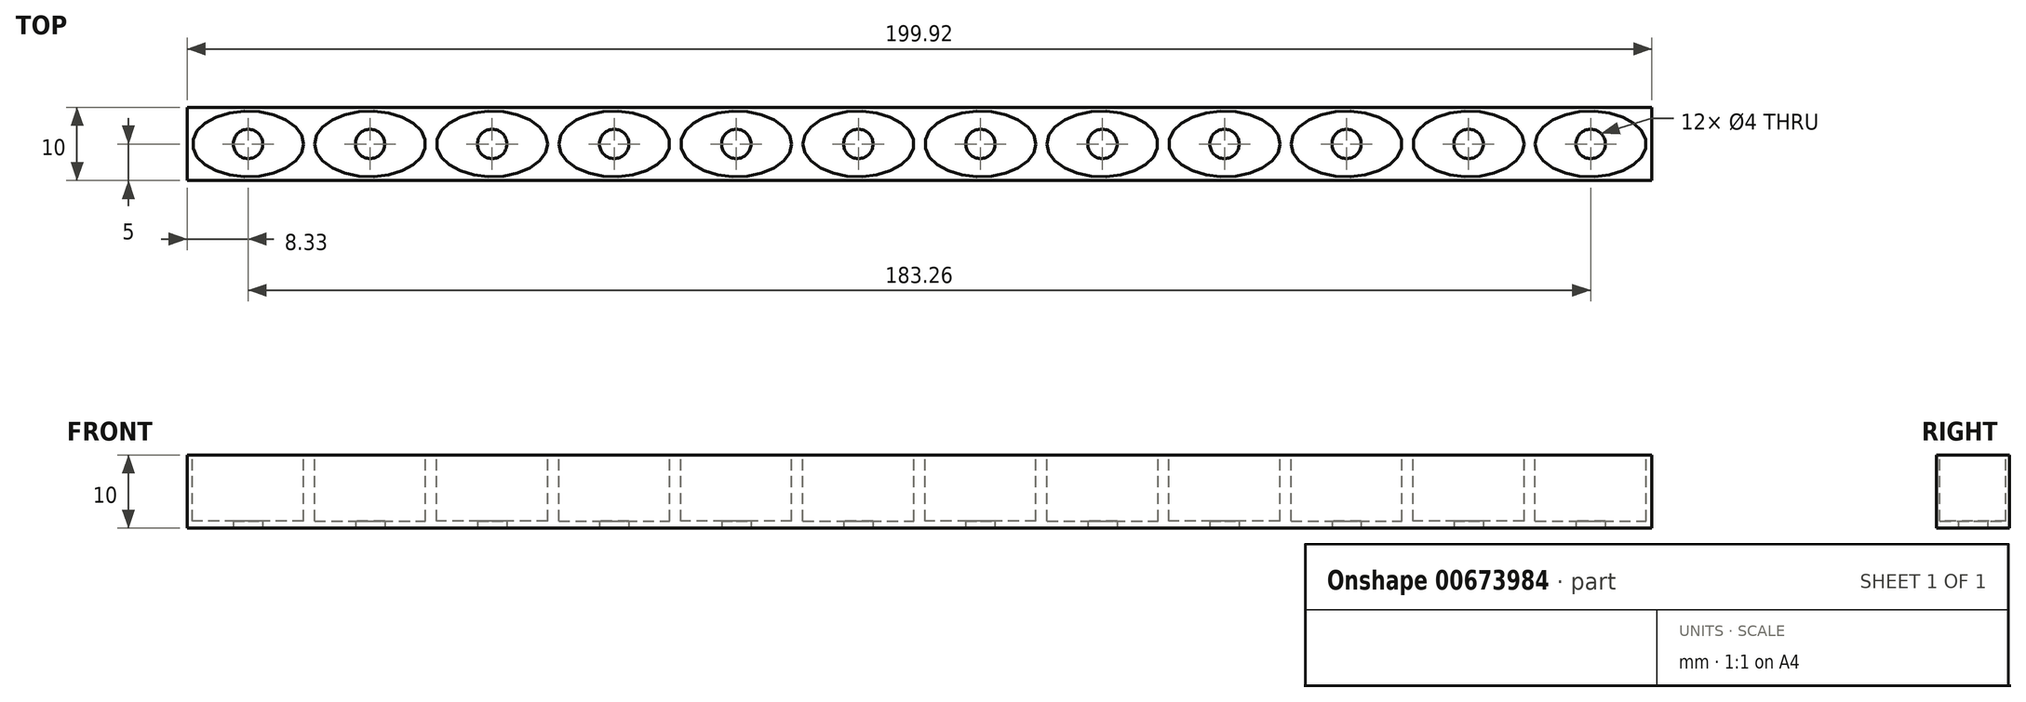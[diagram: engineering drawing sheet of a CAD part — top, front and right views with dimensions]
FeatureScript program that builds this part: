
annotation { "Feature Type Name" : "Feature", "Feature Type Description" : "" }
export const myFeature = defineFeature(function(context is Context, id is Id, definition is map)
    precondition{}
    {
        {
            var Q0;
            Q0=qCreatedBy(makeId("Front.planeOp"),FACE);
            var sketch = newSketch(context, id + "F0", { "sketchPlane" : qUnion([Q0])});
            skLineSegment(sketch, "E0.bottom", {"start": v(-8.33, 5) * mm, "end": v(8.33, 5) * mm});
            skLineSegment(sketch, "E0.top", {"start": v(-8.33, -5) * mm, "end": v(8.33, -5) * mm});
            skLineSegment(sketch, "E0.left", {"start": v(-8.33, 5) * mm, "end": v(-8.33, -5) * mm});
            skLineSegment(sketch, "E0.right", {"start": v(8.33, 5) * mm, "end": v(8.33, -5) * mm});
            skPoint(sketch, "E0.middle", {"position": v(0, 0) * mm});
            skCircle(sketch, "E1", {"center": v(0, 0) * mm, "radius": 2 * mm});
            skLineSegment(sketch, "E2.bottom", {"start": v(-24.99, 5) * mm, "end": v(-8.33, 5) * mm});
            skLineSegment(sketch, "E2.top", {"start": v(-24.99, -5) * mm, "end": v(-8.33, -5) * mm});
            skLineSegment(sketch, "E2.left", {"start": v(-24.99, 5) * mm, "end": v(-24.99, -5) * mm});
            skPoint(sketch, "E2.middle", {"position": v(-16.66, 0) * mm});
            skCircle(sketch, "E3", {"center": v(-16.66, 0) * mm, "radius": 2 * mm});
            skLineSegment(sketch, "E4.bottom", {"start": v(8.33, 5) * mm, "end": v(25, 5) * mm});
            skLineSegment(sketch, "E4.top", {"start": v(8.33, -5) * mm, "end": v(25, -5) * mm});
            skLineSegment(sketch, "E4.right", {"start": v(25, 5) * mm, "end": v(25, -5) * mm});
            skPoint(sketch, "E4.middle", {"position": v(16.66, 0) * mm});
            skCircle(sketch, "E5", {"center": v(16.66, 0) * mm, "radius": 2 * mm});
            skLineSegment(sketch, "E6.bottom", {"start": v(-58.31, 5) * mm, "end": v(-41.65, 5) * mm});
            skLineSegment(sketch, "E6.top", {"start": v(-58.3, -5) * mm, "end": v(-41.65, -5) * mm});
            skLineSegment(sketch, "E6.left", {"start": v(-58.3, 5) * mm, "end": v(-58.3, -5) * mm});
            skLineSegment(sketch, "E6.right", {"start": v(-41.65, 5) * mm, "end": v(-41.65, -5) * mm});
            skPoint(sketch, "E6.middle", {"position": v(-49.98, 0) * mm});
            skCircle(sketch, "E7", {"center": v(-49.98, 0) * mm, "radius": 2 * mm});
            skLineSegment(sketch, "E8.bottom", {"start": v(-74.97, 5) * mm, "end": v(-58.31, 5) * mm});
            skLineSegment(sketch, "E8.top", {"start": v(-74.97, -5) * mm, "end": v(-58.3, -5) * mm});
            skLineSegment(sketch, "E8.left", {"start": v(-74.97, 5) * mm, "end": v(-74.97, -5) * mm});
            skPoint(sketch, "E8.middle", {"position": v(-66.64, 0) * mm});
            skCircle(sketch, "E9", {"center": v(-66.64, 0) * mm, "radius": 2 * mm});
            skLineSegment(sketch, "E10.bottom", {"start": v(-41.65, 5) * mm, "end": v(-24.99, 5) * mm});
            skLineSegment(sketch, "E10.top", {"start": v(-41.65, -5) * mm, "end": v(-25, -5) * mm});
            skPoint(sketch, "E10.middle", {"position": v(-33.32, 0) * mm});
            skCircle(sketch, "E11", {"center": v(-33.32, 0) * mm, "radius": 2 * mm});
            skLineSegment(sketch, "E12.bottom", {"start": v(41.65, 5) * mm, "end": v(58.31, 5) * mm});
            skLineSegment(sketch, "E12.top", {"start": v(41.65, -5) * mm, "end": v(58.31, -5) * mm});
            skLineSegment(sketch, "E12.left", {"start": v(41.65, 5) * mm, "end": v(41.65, -5) * mm});
            skLineSegment(sketch, "E12.right", {"start": v(58.31, 5) * mm, "end": v(58.31, -5) * mm});
            skPoint(sketch, "E12.middle", {"position": v(49.98, 0) * mm});
            skCircle(sketch, "E13", {"center": v(49.98, 0) * mm, "radius": 2 * mm});
            skLineSegment(sketch, "E14.bottom", {"start": v(25, 5) * mm, "end": v(41.65, 5) * mm});
            skLineSegment(sketch, "E14.top", {"start": v(25, -5) * mm, "end": v(41.65, -5) * mm});
            skPoint(sketch, "E14.middle", {"position": v(33.32, 0) * mm});
            skCircle(sketch, "E15", {"center": v(33.32, 0) * mm, "radius": 2 * mm});
            skLineSegment(sketch, "E16.bottom", {"start": v(58.31, 5) * mm, "end": v(74.97, 5) * mm});
            skLineSegment(sketch, "E16.top", {"start": v(58.31, -5) * mm, "end": v(74.97, -5) * mm});
            skLineSegment(sketch, "E16.right", {"start": v(74.97, 5) * mm, "end": v(74.97, -5) * mm});
            skPoint(sketch, "E16.middle", {"position": v(66.64, 0) * mm});
            skCircle(sketch, "E17", {"center": v(66.64, 0) * mm, "radius": 2 * mm});
            skLineSegment(sketch, "E18.bottom", {"start": v(-108.29, 5) * mm, "end": v(-91.63, 5) * mm});
            skLineSegment(sketch, "E18.top", {"start": v(-108.29, -5) * mm, "end": v(-91.63, -5) * mm});
            skLineSegment(sketch, "E18.left", {"start": v(-108.29, 5) * mm, "end": v(-108.29, -5) * mm});
            skLineSegment(sketch, "E18.right", {"start": v(-91.63, 5) * mm, "end": v(-91.63, -5) * mm});
            skPoint(sketch, "E18.middle", {"position": v(-99.96, 0) * mm});
            skCircle(sketch, "E19", {"center": v(-99.96, 0) * mm, "radius": 2 * mm});
            skLineSegment(sketch, "E20.bottom", {"start": v(-124.95, 5) * mm, "end": v(-108.29, 5) * mm});
            skLineSegment(sketch, "E20.top", {"start": v(-124.95, -5) * mm, "end": v(-108.29, -5) * mm});
            skLineSegment(sketch, "E20.left", {"start": v(-124.95, 5) * mm, "end": v(-124.95, -5) * mm});
            skPoint(sketch, "E20.middle", {"position": v(-116.62, 0) * mm});
            skCircle(sketch, "E21", {"center": v(-116.62, 0) * mm, "radius": 2 * mm});
            skLineSegment(sketch, "E22.bottom", {"start": v(-91.63, 5) * mm, "end": v(-74.97, 5) * mm});
            skLineSegment(sketch, "E22.top", {"start": v(-91.63, -5) * mm, "end": v(-74.97, -5) * mm});
            skPoint(sketch, "E22.middle", {"position": v(-83.3, 0) * mm});
            skCircle(sketch, "E23", {"center": v(-83.3, 0) * mm, "radius": 2 * mm});
            skSolve(sketch);
        }
        {
            var Q0;
            Q0 = qSketchRegion(id + "F0", true);
            extrude(context, id + "F1", {"entities" : qUnion([Q0]), "depth" : 10 * mm, "offsetDistance" : 25 * mm});
        }
        {
            var Q0;
            Q0=makeQuery(id+"F1.opExtrude","CAP_FACE",FACE,{"disambiguationData":[OSD([sQuery(id+"F0.wireOp",EDGE,"E0.bottom"),sQuery(id+"F0.wireOp",EDGE,"E0.top"),sQuery(id+"F0.wireOp",EDGE,"E1"),sQuery(id+"F0.wireOp",EDGE,"E2.bottom"),sQuery(id+"F0.wireOp",EDGE,"E2.top"),sQuery(id+"F0.wireOp",EDGE,"E3"),sQuery(id+"F0.wireOp",EDGE,"E4.bottom"),sQuery(id+"F0.wireOp",EDGE,"E4.top"),sQuery(id+"F0.wireOp",EDGE,"E5"),sQuery(id+"F0.wireOp",EDGE,"E6.bottom"),sQuery(id+"F0.wireOp",EDGE,"E6.top"),sQuery(id+"F0.wireOp",EDGE,"E7"),sQuery(id+"F0.wireOp",EDGE,"E8.bottom"),sQuery(id+"F0.wireOp",EDGE,"E8.top"),sQuery(id+"F0.wireOp",EDGE,"E9"),sQuery(id+"F0.wireOp",EDGE,"E10.bottom"),sQuery(id+"F0.wireOp",EDGE,"E10.top"),sQuery(id+"F0.wireOp",EDGE,"E11"),sQuery(id+"F0.wireOp",EDGE,"E12.bottom"),sQuery(id+"F0.wireOp",EDGE,"E12.top"),sQuery(id+"F0.wireOp",EDGE,"E13"),sQuery(id+"F0.wireOp",EDGE,"E14.bottom"),sQuery(id+"F0.wireOp",EDGE,"E14.top"),sQuery(id+"F0.wireOp",EDGE,"E15"),sQuery(id+"F0.wireOp",EDGE,"E16.bottom"),sQuery(id+"F0.wireOp",EDGE,"E16.top"),sQuery(id+"F0.wireOp",EDGE,"E16.right"),sQuery(id+"F0.wireOp",EDGE,"E17"),sQuery(id+"F0.wireOp",EDGE,"E18.bottom"),sQuery(id+"F0.wireOp",EDGE,"E18.top"),sQuery(id+"F0.wireOp",EDGE,"E19"),sQuery(id+"F0.wireOp",EDGE,"E20.bottom"),sQuery(id+"F0.wireOp",EDGE,"E20.top"),sQuery(id+"F0.wireOp",EDGE,"E20.left"),sQuery(id+"F0.wireOp",EDGE,"E21"),sQuery(id+"F0.wireOp",EDGE,"E22.bottom"),sQuery(id+"F0.wireOp",EDGE,"E22.top"),sQuery(id+"F0.wireOp",EDGE,"E23")])],"isStart":false});
            cPlane(context, id + "F2", {"entities" : qUnion([Q0]), "cplaneType" : CPlaneType.OFFSET, "offset" : 0 * mm, "width" : 150 * mm, "height" : 150 * mm});
        }
        {
            var Q0;
            Q0=qCreatedBy(id+"F2.planeOp",FACE);
            var sketch = newSketch(context, id + "F3", { "sketchPlane" : qUnion([Q0])});
            skEllipse(sketch, "E24", {"center": v(0, 0) * mm, "majorRadius": 7.58 * mm, "minorRadius": 4.5 * mm, "majorAxis": v(-1, 0)});
            skEllipse(sketch, "E25.MirrorC", {"center": v(16.66, 0) * mm, "majorRadius": 7.58 * mm, "minorRadius": 4.5 * mm, "majorAxis": v(1, 0)});
            skEllipse(sketch, "E26.MirrorC", {"center": v(33.32, 0) * mm, "majorRadius": 7.58 * mm, "minorRadius": 4.5 * mm, "majorAxis": v(-1, 0)});
            skEllipse(sketch, "E27.MirrorC", {"center": v(49.98, 0) * mm, "majorRadius": 7.58 * mm, "minorRadius": 4.5 * mm, "majorAxis": v(1, 0)});
            skEllipse(sketch, "E28.MirrorC", {"center": v(66.64, 0) * mm, "majorRadius": 7.58 * mm, "minorRadius": 4.5 * mm, "majorAxis": v(-1, 0)});
            skEllipse(sketch, "E29.MirrorC", {"center": v(-16.66, 0) * mm, "majorRadius": 7.58 * mm, "minorRadius": 4.5 * mm, "majorAxis": v(1, 0)});
            skEllipse(sketch, "E30.MirrorC", {"center": v(-33.32, 0) * mm, "majorRadius": 7.58 * mm, "minorRadius": 4.5 * mm, "majorAxis": v(-1, 0)});
            skEllipse(sketch, "E31.MirrorC", {"center": v(-49.98, 0) * mm, "majorRadius": 7.58 * mm, "minorRadius": 4.5 * mm, "majorAxis": v(1, 0)});
            skEllipse(sketch, "E32.MirrorC", {"center": v(-66.64, 0) * mm, "majorRadius": 7.58 * mm, "minorRadius": 4.5 * mm, "majorAxis": v(-1, 0)});
            skEllipse(sketch, "E33.MirrorC", {"center": v(-83.3, 0) * mm, "majorRadius": 7.58 * mm, "minorRadius": 4.5 * mm, "majorAxis": v(1, 0)});
            skEllipse(sketch, "E34.MirrorC", {"center": v(-99.96, 0) * mm, "majorRadius": 7.58 * mm, "minorRadius": 4.5 * mm, "majorAxis": v(-1, 0)});
            skEllipse(sketch, "E35.MirrorC", {"center": v(-116.62, 0) * mm, "majorRadius": 7.58 * mm, "minorRadius": 4.5 * mm, "majorAxis": v(1, 0)});
            skSolve(sketch);
        }
        {
            var Q0;
            Q0=makeQuery(id+"F3.imprint","IMPRINT",FACE,{"disambiguationData":[TD([[makeQuery(id+"F3.imprint","IMPRINT",EDGE,{"derivedFrom":sQuery(id+"F3.wireOp",EDGE,"E33.MirrorC")}),1.0]])]});
            var Q1;
            Q1=makeQuery(id+"F3.imprint","IMPRINT",FACE,{"disambiguationData":[TD([[makeQuery(id+"F3.imprint","IMPRINT",EDGE,{"derivedFrom":sQuery(id+"F3.wireOp",EDGE,"E35.MirrorC")}),1.0]])]});
            var Q2;
            Q2=makeQuery(id+"F3.imprint","IMPRINT",FACE,{"disambiguationData":[TD([[makeQuery(id+"F3.imprint","IMPRINT",EDGE,{"derivedFrom":sQuery(id+"F3.wireOp",EDGE,"E34.MirrorC")}),1.0]])]});
            var Q3;
            Q3=makeQuery(id+"F3.imprint","IMPRINT",FACE,{"disambiguationData":[TD([[makeQuery(id+"F3.imprint","IMPRINT",EDGE,{"derivedFrom":sQuery(id+"F3.wireOp",EDGE,"E32.MirrorC")}),1.0]])]});
            var Q4;
            Q4=makeQuery(id+"F3.imprint","IMPRINT",FACE,{"disambiguationData":[TD([[makeQuery(id+"F3.imprint","IMPRINT",EDGE,{"derivedFrom":sQuery(id+"F3.wireOp",EDGE,"E31.MirrorC")}),1.0]])]});
            var Q5;
            Q5=makeQuery(id+"F3.imprint","IMPRINT",FACE,{"disambiguationData":[TD([[makeQuery(id+"F3.imprint","IMPRINT",EDGE,{"derivedFrom":sQuery(id+"F3.wireOp",EDGE,"E30.MirrorC")}),1.0]])]});
            var Q6;
            Q6=makeQuery(id+"F3.imprint","IMPRINT",FACE,{"disambiguationData":[TD([[makeQuery(id+"F3.imprint","IMPRINT",EDGE,{"derivedFrom":sQuery(id+"F3.wireOp",EDGE,"E29.MirrorC")}),1.0]])]});
            var Q7;
            Q7=makeQuery(id+"F3.imprint","IMPRINT",FACE,{"disambiguationData":[TD([[makeQuery(id+"F3.imprint","IMPRINT",EDGE,{"derivedFrom":sQuery(id+"F3.wireOp",EDGE,"E24")}),1.0]])]});
            var Q8;
            Q8=makeQuery(id+"F3.imprint","IMPRINT",FACE,{"disambiguationData":[TD([[makeQuery(id+"F3.imprint","IMPRINT",EDGE,{"derivedFrom":sQuery(id+"F3.wireOp",EDGE,"E25.MirrorC")}),1.0]])]});
            var Q9;
            Q9=makeQuery(id+"F3.imprint","IMPRINT",FACE,{"disambiguationData":[TD([[makeQuery(id+"F3.imprint","IMPRINT",EDGE,{"derivedFrom":sQuery(id+"F3.wireOp",EDGE,"E26.MirrorC")}),1.0]])]});
            var Q10;
            Q10=makeQuery(id+"F3.imprint","IMPRINT",FACE,{"disambiguationData":[TD([[makeQuery(id+"F3.imprint","IMPRINT",EDGE,{"derivedFrom":sQuery(id+"F3.wireOp",EDGE,"E27.MirrorC")}),1.0]])]});
            var Q11;
            Q11=makeQuery(id+"F3.imprint","IMPRINT",FACE,{"disambiguationData":[TD([[makeQuery(id+"F3.imprint","IMPRINT",EDGE,{"derivedFrom":sQuery(id+"F3.wireOp",EDGE,"E28.MirrorC")}),1.0]])]});
            var Q12;
            Q12=sQuery(id+"F0.wireOp",EDGE,"E19");
            var Q13;
            Q13=sQuery(id+"F3.wireOp",EDGE,"E34.MirrorC");
            extrude(context, id + "F4", {"entities" : qUnion([Q0, Q1, Q2, Q3, Q4, Q5, Q6, Q7, Q8, Q9, Q10, Q11]), "operationType" : NewBodyOperationType.REMOVE, "surfaceEntities" : qUnion([Q12, Q13]), "oppositeDirection" : true, "depth" : 9 * mm, "offsetDistance" : 25 * mm});
        }
        {
            var Q0;
            Q0=makeQuery(id+"F1.opExtrude","SWEPT_BODY",BODY,{"disambiguationData":[OSD([sQuery(id+"F0.wireOp",EDGE,"E0.bottom"),sQuery(id+"F0.wireOp",EDGE,"E0.top"),sQuery(id+"F0.wireOp",EDGE,"E1"),sQuery(id+"F0.wireOp",EDGE,"E2.bottom"),sQuery(id+"F0.wireOp",EDGE,"E2.top"),sQuery(id+"F0.wireOp",EDGE,"E3"),sQuery(id+"F0.wireOp",EDGE,"E4.bottom"),sQuery(id+"F0.wireOp",EDGE,"E4.top"),sQuery(id+"F0.wireOp",EDGE,"E5"),sQuery(id+"F0.wireOp",EDGE,"E6.bottom"),sQuery(id+"F0.wireOp",EDGE,"E6.top"),sQuery(id+"F0.wireOp",EDGE,"E7"),sQuery(id+"F0.wireOp",EDGE,"E8.bottom"),sQuery(id+"F0.wireOp",EDGE,"E8.top"),sQuery(id+"F0.wireOp",EDGE,"E9"),sQuery(id+"F0.wireOp",EDGE,"E10.bottom"),sQuery(id+"F0.wireOp",EDGE,"E10.top"),sQuery(id+"F0.wireOp",EDGE,"E11"),sQuery(id+"F0.wireOp",EDGE,"E12.bottom"),sQuery(id+"F0.wireOp",EDGE,"E12.top"),sQuery(id+"F0.wireOp",EDGE,"E13"),sQuery(id+"F0.wireOp",EDGE,"E14.bottom"),sQuery(id+"F0.wireOp",EDGE,"E14.top"),sQuery(id+"F0.wireOp",EDGE,"E15"),sQuery(id+"F0.wireOp",EDGE,"E16.bottom"),sQuery(id+"F0.wireOp",EDGE,"E16.top"),sQuery(id+"F0.wireOp",EDGE,"E16.right"),sQuery(id+"F0.wireOp",EDGE,"E17"),sQuery(id+"F0.wireOp",EDGE,"E18.bottom"),sQuery(id+"F0.wireOp",EDGE,"E18.top"),sQuery(id+"F0.wireOp",EDGE,"E19"),sQuery(id+"F0.wireOp",EDGE,"E20.bottom"),sQuery(id+"F0.wireOp",EDGE,"E20.top"),sQuery(id+"F0.wireOp",EDGE,"E20.left"),sQuery(id+"F0.wireOp",EDGE,"E21"),sQuery(id+"F0.wireOp",EDGE,"E22.bottom"),sQuery(id+"F0.wireOp",EDGE,"E22.top"),sQuery(id+"F0.wireOp",EDGE,"E23")])]});
            var Q1;
            Q1=sQuery(id+"F0.wireOp",EDGE,"E20.top");
            transform(context, id + "F5", {"entities" : qUnion([Q0]), "transformType" : TransformType.ROTATION, "transformAxis" : qUnion([Q1]), "angle" : 90 * degree, "oppositeDirection" : true, "makeCopy" : false});
        }
    });
